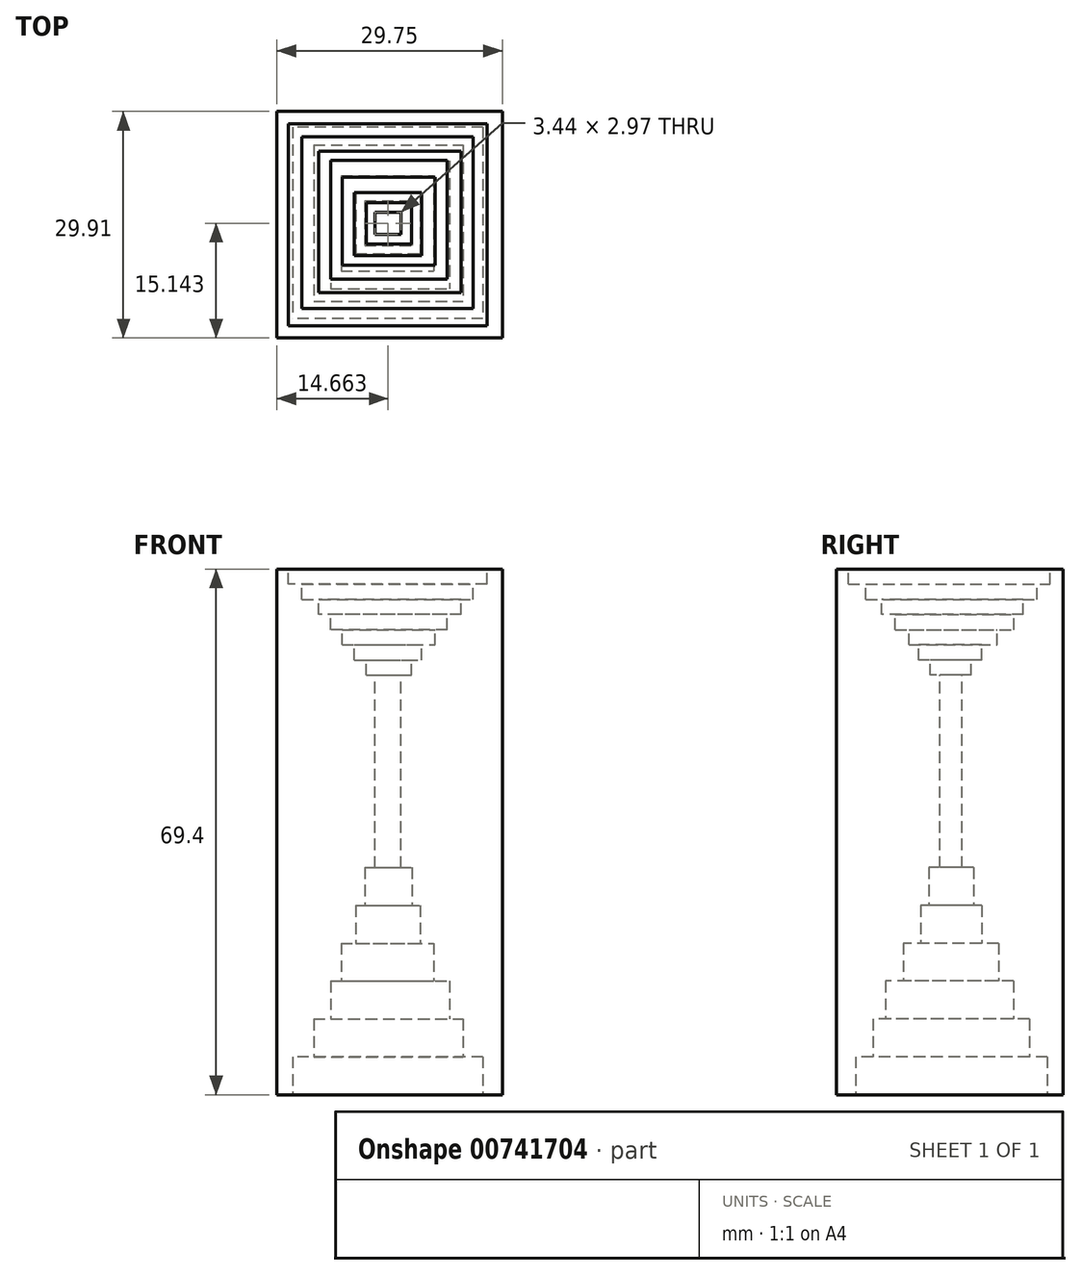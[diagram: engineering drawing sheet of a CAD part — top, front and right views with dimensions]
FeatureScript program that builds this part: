
annotation { "Feature Type Name" : "Feature", "Feature Type Description" : "" }
export const myFeature = defineFeature(function(context is Context, id is Id, definition is map)
    precondition{}
    {
        {
            var Q0;
            Q0=qCreatedBy(makeId("Top.planeOp"),FACE);
            var sketch = newSketch(context, id + "F0", { "sketchPlane" : qUnion([Q0])});
            skLineSegment(sketch, "E0.bottom", {"start": v(11.57, -13.66) * mm, "end": v(41.32, -13.66) * mm});
            skLineSegment(sketch, "E0.top", {"start": v(11.57, 16.25) * mm, "end": v(41.32, 16.25) * mm});
            skLineSegment(sketch, "E0.left", {"start": v(11.57, -13.66) * mm, "end": v(11.57, 16.25) * mm});
            skLineSegment(sketch, "E0.right", {"start": v(41.32, -13.66) * mm, "end": v(41.32, 16.25) * mm});
            skSolve(sketch);
        }
        {
            var Q0;
            Q0=makeQuery(id+"F0.imprint","IMPRINT",FACE,{"disambiguationData":[TD([[makeQuery(id+"F0.imprint","IMPRINT",EDGE,{"derivedFrom":sQuery(id+"F0.wireOp",EDGE,"E0.bottom")}),1.0]])]});
            extrude(context, id + "F1", {"entities" : qUnion([Q0]), "depth" : 69.4 * mm, "offsetDistance" : 25 * mm});
        }
        {
            var Q0;
            Q0=makeQuery(id+"F1.opExtrude","CAP_FACE",FACE,{"disambiguationData":[OSD([sQuery(id+"F0.wireOp",EDGE,"E0.bottom"),sQuery(id+"F0.wireOp",EDGE,"E0.top"),sQuery(id+"F0.wireOp",EDGE,"E0.left"),sQuery(id+"F0.wireOp",EDGE,"E0.right")])],"isStart":false});
            var sketch = newSketch(context, id + "F2", { "sketchPlane" : qUnion([Q0])});
            skLineSegment(sketch, "E1.bottom", {"start": v(39.29, -12.06) * mm, "end": v(13.06, -12.06) * mm});
            skLineSegment(sketch, "E1.top", {"start": v(39.29, 14.6) * mm, "end": v(13.06, 14.6) * mm});
            skLineSegment(sketch, "E1.left", {"start": v(39.29, -12.06) * mm, "end": v(39.29, 14.6) * mm});
            skLineSegment(sketch, "E1.right", {"start": v(13.06, -12.06) * mm, "end": v(13.06, 14.6) * mm});
            skSolve(sketch);
        }
        {
            var Q0;
            Q0=makeQuery(id+"F2.imprint","IMPRINT",FACE,{"disambiguationData":[TD([[makeQuery(id+"F2.imprint","IMPRINT",EDGE,{"derivedFrom":sQuery(id+"F2.wireOp",EDGE,"E1.bottom")}),-1.0]])]});
            extrude(context, id + "F3", {"entities" : qUnion([Q0]), "operationType" : NewBodyOperationType.REMOVE, "oppositeDirection" : true, "depth" : 2 * mm, "offsetDistance" : 25 * mm});
        }
        {
            var Q0;
            Q0=makeQuery(id+"F3.boolean.opBoolean","COPY",FACE,{"derivedFrom":makeQuery(id+"F3.opExtrude","CAP_FACE",FACE,{"disambiguationData":[OSD([sQuery(id+"F2.wireOp",EDGE,"E1.bottom"),sQuery(id+"F2.wireOp",EDGE,"E1.top"),sQuery(id+"F2.wireOp",EDGE,"E1.left"),sQuery(id+"F2.wireOp",EDGE,"E1.right")])],"isStart":false})});
            var sketch = newSketch(context, id + "F4", { "sketchPlane" : qUnion([Q0])});
            skLineSegment(sketch, "E2.bottom", {"start": v(14.87, -9.76) * mm, "end": v(37.5, -9.76) * mm});
            skLineSegment(sketch, "E2.top", {"start": v(14.87, 12.88) * mm, "end": v(37.5, 12.88) * mm});
            skLineSegment(sketch, "E2.left", {"start": v(14.87, -9.76) * mm, "end": v(14.87, 12.88) * mm});
            skLineSegment(sketch, "E2.right", {"start": v(37.5, -9.76) * mm, "end": v(37.5, 12.88) * mm});
            skSolve(sketch);
        }
        {
            var Q0;
            Q0=makeQuery(id+"F4.imprint","IMPRINT",FACE,{"disambiguationData":[TD([[makeQuery(id+"F4.imprint","IMPRINT",EDGE,{"derivedFrom":sQuery(id+"F4.wireOp",EDGE,"E2.bottom")}),1.0]])]});
            extrude(context, id + "F5", {"entities" : qUnion([Q0]), "operationType" : NewBodyOperationType.REMOVE, "oppositeDirection" : true, "depth" : 2 * mm, "offsetDistance" : 25 * mm});
        }
        {
            var Q0;
            Q0=makeQuery(id+"F5.boolean.opBoolean","COPY",FACE,{"derivedFrom":makeQuery(id+"F5.opExtrude","CAP_FACE",FACE,{"disambiguationData":[OSD([sQuery(id+"F4.wireOp",EDGE,"E2.bottom"),sQuery(id+"F4.wireOp",EDGE,"E2.top"),sQuery(id+"F4.wireOp",EDGE,"E2.left"),sQuery(id+"F4.wireOp",EDGE,"E2.right")])],"isStart":false})});
            var sketch = newSketch(context, id + "F6", { "sketchPlane" : qUnion([Q0])});
            skLineSegment(sketch, "E3.bottom", {"start": v(35.9, 11.02) * mm, "end": v(17.1, 11.02) * mm});
            skLineSegment(sketch, "E3.top", {"start": v(35.9, -7.7) * mm, "end": v(17.1, -7.7) * mm});
            skLineSegment(sketch, "E3.left", {"start": v(35.9, 11.02) * mm, "end": v(35.9, -7.7) * mm});
            skLineSegment(sketch, "E3.right", {"start": v(17.1, 11.02) * mm, "end": v(17.1, -7.7) * mm});
            skSolve(sketch);
        }
        {
            var Q0;
            Q0=makeQuery(id+"F6.imprint","IMPRINT",FACE,{"disambiguationData":[TD([[makeQuery(id+"F6.imprint","IMPRINT",EDGE,{"derivedFrom":sQuery(id+"F6.wireOp",EDGE,"E3.bottom")}),1.0]])]});
            extrude(context, id + "F7", {"entities" : qUnion([Q0]), "operationType" : NewBodyOperationType.REMOVE, "oppositeDirection" : true, "depth" : 2 * mm, "offsetDistance" : 25 * mm});
        }
        {
            var Q0;
            Q0=makeQuery(id+"F7.boolean.opBoolean","COPY",FACE,{"derivedFrom":makeQuery(id+"F7.opExtrude","CAP_FACE",FACE,{"disambiguationData":[OSD([sQuery(id+"F6.wireOp",EDGE,"E3.bottom"),sQuery(id+"F6.wireOp",EDGE,"E3.top"),sQuery(id+"F6.wireOp",EDGE,"E3.left"),sQuery(id+"F6.wireOp",EDGE,"E3.right")])],"isStart":false})});
            var sketch = newSketch(context, id + "F8", { "sketchPlane" : qUnion([Q0])});
            skLineSegment(sketch, "E4.bottom", {"start": v(34.06, -5.88) * mm, "end": v(18.64, -5.88) * mm});
            skLineSegment(sketch, "E4.top", {"start": v(34.06, 9.79) * mm, "end": v(18.64, 9.79) * mm});
            skLineSegment(sketch, "E4.left", {"start": v(34.06, -5.88) * mm, "end": v(34.06, 9.79) * mm});
            skLineSegment(sketch, "E4.right", {"start": v(18.64, -5.88) * mm, "end": v(18.64, 9.79) * mm});
            skSolve(sketch);
        }
        {
            var Q0;
            Q0=makeQuery(id+"F8.imprint","IMPRINT",FACE,{"disambiguationData":[TD([[makeQuery(id+"F8.imprint","IMPRINT",EDGE,{"derivedFrom":sQuery(id+"F8.wireOp",EDGE,"E4.bottom")}),-1.0]])]});
            extrude(context, id + "F9", {"entities" : qUnion([Q0]), "operationType" : NewBodyOperationType.REMOVE, "oppositeDirection" : true, "depth" : 2 * mm, "offsetDistance" : 25 * mm});
        }
        {
            var Q0;
            Q0=makeQuery(id+"F9.boolean.opBoolean","COPY",FACE,{"derivedFrom":makeQuery(id+"F9.opExtrude","CAP_FACE",FACE,{"disambiguationData":[OSD([sQuery(id+"F8.wireOp",EDGE,"E4.bottom"),sQuery(id+"F8.wireOp",EDGE,"E4.top"),sQuery(id+"F8.wireOp",EDGE,"E4.left"),sQuery(id+"F8.wireOp",EDGE,"E4.right")])],"isStart":false})});
            var sketch = newSketch(context, id + "F10", { "sketchPlane" : qUnion([Q0])});
            skLineSegment(sketch, "E5.bottom", {"start": v(20.19, -4.04) * mm, "end": v(32.43, -4.04) * mm});
            skLineSegment(sketch, "E5.top", {"start": v(20.19, 7.55) * mm, "end": v(32.43, 7.55) * mm});
            skLineSegment(sketch, "E5.left", {"start": v(20.19, -4.04) * mm, "end": v(20.19, 7.55) * mm});
            skLineSegment(sketch, "E5.right", {"start": v(32.43, -4.04) * mm, "end": v(32.43, 7.55) * mm});
            skSolve(sketch);
        }
        {
            var Q0;
            Q0=makeQuery(id+"F10.imprint","IMPRINT",FACE,{"disambiguationData":[TD([[makeQuery(id+"F10.imprint","IMPRINT",EDGE,{"derivedFrom":sQuery(id+"F10.wireOp",EDGE,"E5.bottom")}),1.0]])]});
            extrude(context, id + "F11", {"entities" : qUnion([Q0]), "operationType" : NewBodyOperationType.REMOVE, "oppositeDirection" : true, "depth" : 2 * mm, "offsetDistance" : 25 * mm});
        }
        {
            var Q0;
            Q0=makeQuery(id+"F11.boolean.opBoolean","COPY",FACE,{"derivedFrom":makeQuery(id+"F11.opExtrude","CAP_FACE",FACE,{"disambiguationData":[OSD([sQuery(id+"F10.wireOp",EDGE,"E5.bottom"),sQuery(id+"F10.wireOp",EDGE,"E5.top"),sQuery(id+"F10.wireOp",EDGE,"E5.left"),sQuery(id+"F10.wireOp",EDGE,"E5.right")])],"isStart":false})});
            var sketch = newSketch(context, id + "F12", { "sketchPlane" : qUnion([Q0])});
            skLineSegment(sketch, "E6.bottom", {"start": v(21.78, 5.53) * mm, "end": v(30.65, 5.53) * mm});
            skLineSegment(sketch, "E6.top", {"start": v(21.78, -2.78) * mm, "end": v(30.65, -2.78) * mm});
            skLineSegment(sketch, "E6.left", {"start": v(21.78, 5.53) * mm, "end": v(21.78, -2.78) * mm});
            skLineSegment(sketch, "E6.right", {"start": v(30.65, 5.53) * mm, "end": v(30.65, -2.78) * mm});
            skSolve(sketch);
        }
        {
            var Q0;
            Q0=makeQuery(id+"F12.imprint","IMPRINT",FACE,{"disambiguationData":[TD([[makeQuery(id+"F12.imprint","IMPRINT",EDGE,{"derivedFrom":sQuery(id+"F12.wireOp",EDGE,"E6.bottom")}),-1.0]])]});
            extrude(context, id + "F13", {"entities" : qUnion([Q0]), "operationType" : NewBodyOperationType.REMOVE, "oppositeDirection" : true, "depth" : 2 * mm, "offsetDistance" : 25 * mm});
        }
        {
            var Q0;
            Q0=makeQuery(id+"F13.boolean.opBoolean","COPY",FACE,{"derivedFrom":makeQuery(id+"F13.opExtrude","CAP_FACE",FACE,{"disambiguationData":[OSD([sQuery(id+"F12.wireOp",EDGE,"E6.bottom"),sQuery(id+"F12.wireOp",EDGE,"E6.top"),sQuery(id+"F12.wireOp",EDGE,"E6.left"),sQuery(id+"F12.wireOp",EDGE,"E6.right")])],"isStart":false})});
            var sketch = newSketch(context, id + "F14", { "sketchPlane" : qUnion([Q0])});
            skLineSegment(sketch, "E7.bottom", {"start": v(23.38, 4.18) * mm, "end": v(29.33, 4.18) * mm});
            skLineSegment(sketch, "E7.top", {"start": v(23.38, -1.22) * mm, "end": v(29.33, -1.22) * mm});
            skLineSegment(sketch, "E7.left", {"start": v(23.38, 4.18) * mm, "end": v(23.38, -1.22) * mm});
            skLineSegment(sketch, "E7.right", {"start": v(29.33, 4.18) * mm, "end": v(29.33, -1.22) * mm});
            skSolve(sketch);
        }
        {
            var Q0;
            Q0=makeQuery(id+"F14.imprint","IMPRINT",FACE,{"disambiguationData":[TD([[makeQuery(id+"F14.imprint","IMPRINT",EDGE,{"derivedFrom":sQuery(id+"F14.wireOp",EDGE,"E7.bottom")}),-1.0]])]});
            extrude(context, id + "F15", {"entities" : qUnion([Q0]), "operationType" : NewBodyOperationType.REMOVE, "oppositeDirection" : true, "depth" : 2 * mm, "offsetDistance" : 25 * mm});
        }
        {
            var Q0;
            Q0=makeQuery(id+"F15.boolean.opBoolean","COPY",FACE,{"derivedFrom":makeQuery(id+"F15.opExtrude","CAP_FACE",FACE,{"disambiguationData":[OSD([sQuery(id+"F14.wireOp",EDGE,"E7.bottom"),sQuery(id+"F14.wireOp",EDGE,"E7.top"),sQuery(id+"F14.wireOp",EDGE,"E7.left"),sQuery(id+"F14.wireOp",EDGE,"E7.right")])],"isStart":false})});
            var sketch = newSketch(context, id + "F16", { "sketchPlane" : qUnion([Q0])});
            skLineSegment(sketch, "E8.bottom", {"start": v(24.51, 2.97) * mm, "end": v(27.95, 2.97) * mm});
            skLineSegment(sketch, "E8.top", {"start": v(24.51, 0) * mm, "end": v(27.95, 0) * mm});
            skLineSegment(sketch, "E8.left", {"start": v(24.51, 2.97) * mm, "end": v(24.51, 0) * mm});
            skLineSegment(sketch, "E8.right", {"start": v(27.95, 2.97) * mm, "end": v(27.95, 0) * mm});
            skSolve(sketch);
        }
        {
            var Q0;
            Q0=makeQuery(id+"F16.imprint","IMPRINT",FACE,{"disambiguationData":[TD([[makeQuery(id+"F16.imprint","IMPRINT",EDGE,{"derivedFrom":sQuery(id+"F16.wireOp",EDGE,"E8.bottom")}),-1.0]])]});
            extrude(context, id + "F17", {"entities" : qUnion([Q0]), "operationType" : NewBodyOperationType.REMOVE, "endBound" : BoundingType.THROUGH_ALL, "oppositeDirection" : true, "depth" : 25 * mm, "offsetDistance" : 25 * mm});
        }
        {
            var Q0;
            Q0=makeQuery(id+"F1.opExtrude","CAP_FACE",FACE,{"disambiguationData":[OSD([sQuery(id+"F0.wireOp",EDGE,"E0.bottom"),sQuery(id+"F0.wireOp",EDGE,"E0.top"),sQuery(id+"F0.wireOp",EDGE,"E0.left"),sQuery(id+"F0.wireOp",EDGE,"E0.right")])],"isStart":true});
            var sketch = newSketch(context, id + "F18", { "sketchPlane" : qUnion([Q0])});
            skLineSegment(sketch, "E9.bottom", {"start": v(38.76, -14.2) * mm, "end": v(13.65, -14.2) * mm});
            skLineSegment(sketch, "E9.top", {"start": v(38.76, 11.11) * mm, "end": v(13.65, 11.11) * mm});
            skLineSegment(sketch, "E9.left", {"start": v(38.76, -14.2) * mm, "end": v(38.76, 11.11) * mm});
            skLineSegment(sketch, "E9.right", {"start": v(13.65, -14.2) * mm, "end": v(13.65, 11.11) * mm});
            skSolve(sketch);
        }
        {
            var Q0;
            Q0=makeQuery(id+"F18.imprint","IMPRINT",FACE,{"disambiguationData":[TD([[makeQuery(id+"F18.imprint","IMPRINT",EDGE,{"derivedFrom":sQuery(id+"F18.wireOp",EDGE,"E9.bottom")}),-1.0]])]});
            extrude(context, id + "F19", {"entities" : qUnion([Q0]), "operationType" : NewBodyOperationType.REMOVE, "oppositeDirection" : true, "depth" : 5 * mm, "offsetDistance" : 25 * mm});
        }
        {
            var Q0;
            Q0=makeQuery(id+"F19.boolean.opBoolean","COPY",FACE,{"derivedFrom":makeQuery(id+"F19.opExtrude","CAP_FACE",FACE,{"disambiguationData":[OSD([sQuery(id+"F0.wireOp",EDGE,"E0.bottom"),sQuery(id+"F0.wireOp",EDGE,"E0.top"),sQuery(id+"F0.wireOp",EDGE,"E0.left"),sQuery(id+"F0.wireOp",EDGE,"E0.right"),sQuery(id+"F16.wireOp",EDGE,"E8.bottom"),sQuery(id+"F16.wireOp",EDGE,"E8.top"),sQuery(id+"F16.wireOp",EDGE,"E8.left"),sQuery(id+"F16.wireOp",EDGE,"E8.right"),sQuery(id+"F18.wireOp",EDGE,"E9.bottom"),sQuery(id+"F18.wireOp",EDGE,"E9.top"),sQuery(id+"F18.wireOp",EDGE,"E9.left"),sQuery(id+"F18.wireOp",EDGE,"E9.right")])],"isStart":false})});
            var sketch = newSketch(context, id + "F20", { "sketchPlane" : qUnion([Q0])});
            skLineSegment(sketch, "E10.bottom", {"start": v(16.43, -11.84) * mm, "end": v(36.14, -11.84) * mm});
            skLineSegment(sketch, "E10.top", {"start": v(16.43, 8.78) * mm, "end": v(36.14, 8.78) * mm});
            skLineSegment(sketch, "E10.left", {"start": v(16.43, -11.84) * mm, "end": v(16.43, 8.78) * mm});
            skLineSegment(sketch, "E10.right", {"start": v(36.14, -11.84) * mm, "end": v(36.14, 8.78) * mm});
            skSolve(sketch);
        }
        {
            var Q0;
            Q0=makeQuery(id+"F20.imprint","IMPRINT",FACE,{"disambiguationData":[TD([[makeQuery(id+"F20.imprint","IMPRINT",EDGE,{"derivedFrom":sQuery(id+"F20.wireOp",EDGE,"E10.bottom")}),1.0]])]});
            extrude(context, id + "F21", {"entities" : qUnion([Q0]), "operationType" : NewBodyOperationType.REMOVE, "oppositeDirection" : true, "depth" : 5 * mm, "offsetDistance" : 25 * mm});
        }
        {
            var Q0;
            Q0=makeQuery(id+"F21.boolean.opBoolean","COPY",FACE,{"derivedFrom":makeQuery(id+"F21.opExtrude","CAP_FACE",FACE,{"disambiguationData":[OSD([sQuery(id+"F0.wireOp",EDGE,"E0.bottom"),sQuery(id+"F0.wireOp",EDGE,"E0.top"),sQuery(id+"F0.wireOp",EDGE,"E0.left"),sQuery(id+"F0.wireOp",EDGE,"E0.right"),sQuery(id+"F16.wireOp",EDGE,"E8.bottom"),sQuery(id+"F16.wireOp",EDGE,"E8.top"),sQuery(id+"F16.wireOp",EDGE,"E8.left"),sQuery(id+"F16.wireOp",EDGE,"E8.right"),sQuery(id+"F20.wireOp",EDGE,"E10.bottom"),sQuery(id+"F20.wireOp",EDGE,"E10.top"),sQuery(id+"F20.wireOp",EDGE,"E10.left"),sQuery(id+"F20.wireOp",EDGE,"E10.right")])],"isStart":false})});
            var sketch = newSketch(context, id + "F22", { "sketchPlane" : qUnion([Q0])});
            skLineSegment(sketch, "E11.bottom", {"start": v(18.67, -9.73) * mm, "end": v(34.35, -9.73) * mm});
            skLineSegment(sketch, "E11.top", {"start": v(18.67, 7.14) * mm, "end": v(34.35, 7.14) * mm});
            skLineSegment(sketch, "E11.left", {"start": v(18.67, -9.73) * mm, "end": v(18.67, 7.14) * mm});
            skLineSegment(sketch, "E11.right", {"start": v(34.35, -9.73) * mm, "end": v(34.35, 7.14) * mm});
            skSolve(sketch);
        }
        {
            var Q0;
            Q0=makeQuery(id+"F22.imprint","IMPRINT",FACE,{"disambiguationData":[TD([[makeQuery(id+"F22.imprint","IMPRINT",EDGE,{"derivedFrom":sQuery(id+"F22.wireOp",EDGE,"E11.bottom")}),1.0]])]});
            extrude(context, id + "F23", {"entities" : qUnion([Q0]), "operationType" : NewBodyOperationType.REMOVE, "oppositeDirection" : true, "depth" : 5 * mm, "offsetDistance" : 25 * mm});
        }
        {
            var Q0;
            Q0=makeQuery(id+"F23.boolean.opBoolean","COPY",FACE,{"derivedFrom":makeQuery(id+"F23.opExtrude","CAP_FACE",FACE,{"disambiguationData":[OSD([sQuery(id+"F0.wireOp",EDGE,"E0.bottom"),sQuery(id+"F0.wireOp",EDGE,"E0.top"),sQuery(id+"F0.wireOp",EDGE,"E0.left"),sQuery(id+"F0.wireOp",EDGE,"E0.right"),sQuery(id+"F16.wireOp",EDGE,"E8.bottom"),sQuery(id+"F16.wireOp",EDGE,"E8.top"),sQuery(id+"F16.wireOp",EDGE,"E8.left"),sQuery(id+"F16.wireOp",EDGE,"E8.right"),sQuery(id+"F22.wireOp",EDGE,"E11.bottom"),sQuery(id+"F22.wireOp",EDGE,"E11.top"),sQuery(id+"F22.wireOp",EDGE,"E11.left"),sQuery(id+"F22.wireOp",EDGE,"E11.right")])],"isStart":false})});
            var sketch = newSketch(context, id + "F24", { "sketchPlane" : qUnion([Q0])});
            skLineSegment(sketch, "E12.bottom", {"start": v(20.04, -7.76) * mm, "end": v(32.29, -7.76) * mm});
            skLineSegment(sketch, "E12.top", {"start": v(20.04, 4.83) * mm, "end": v(32.29, 4.83) * mm});
            skLineSegment(sketch, "E12.left", {"start": v(20.04, -7.76) * mm, "end": v(20.04, 4.83) * mm});
            skLineSegment(sketch, "E12.right", {"start": v(32.29, -7.76) * mm, "end": v(32.29, 4.83) * mm});
            skSolve(sketch);
        }
        {
            var Q0;
            Q0=makeQuery(id+"F24.imprint","IMPRINT",FACE,{"disambiguationData":[TD([[makeQuery(id+"F24.imprint","IMPRINT",EDGE,{"derivedFrom":sQuery(id+"F24.wireOp",EDGE,"E12.bottom")}),1.0]])]});
            extrude(context, id + "F25", {"entities" : qUnion([Q0]), "operationType" : NewBodyOperationType.REMOVE, "oppositeDirection" : true, "depth" : 5 * mm, "offsetDistance" : 25 * mm});
        }
        {
            var Q0;
            Q0=makeQuery(id+"F25.boolean.opBoolean","COPY",FACE,{"derivedFrom":makeQuery(id+"F25.opExtrude","CAP_FACE",FACE,{"disambiguationData":[OSD([sQuery(id+"F0.wireOp",EDGE,"E0.bottom"),sQuery(id+"F0.wireOp",EDGE,"E0.top"),sQuery(id+"F0.wireOp",EDGE,"E0.left"),sQuery(id+"F0.wireOp",EDGE,"E0.right"),sQuery(id+"F16.wireOp",EDGE,"E8.bottom"),sQuery(id+"F16.wireOp",EDGE,"E8.top"),sQuery(id+"F16.wireOp",EDGE,"E8.left"),sQuery(id+"F16.wireOp",EDGE,"E8.right"),sQuery(id+"F24.wireOp",EDGE,"E12.bottom"),sQuery(id+"F24.wireOp",EDGE,"E12.top"),sQuery(id+"F24.wireOp",EDGE,"E12.left"),sQuery(id+"F24.wireOp",EDGE,"E12.right")])],"isStart":false})});
            var sketch = newSketch(context, id + "F26", { "sketchPlane" : qUnion([Q0])});
            skLineSegment(sketch, "E13.bottom", {"start": v(21.96, -5.55) * mm, "end": v(30.49, -5.55) * mm});
            skLineSegment(sketch, "E13.top", {"start": v(21.96, 2.5) * mm, "end": v(30.49, 2.5) * mm});
            skLineSegment(sketch, "E13.left", {"start": v(21.96, -5.55) * mm, "end": v(21.96, 2.5) * mm});
            skLineSegment(sketch, "E13.right", {"start": v(30.49, -5.55) * mm, "end": v(30.49, 2.5) * mm});
            skSolve(sketch);
        }
        {
            var Q0;
            Q0=makeQuery(id+"F26.imprint","IMPRINT",FACE,{"disambiguationData":[TD([[makeQuery(id+"F26.imprint","IMPRINT",EDGE,{"derivedFrom":sQuery(id+"F26.wireOp",EDGE,"E13.bottom")}),1.0]])]});
            extrude(context, id + "F27", {"entities" : qUnion([Q0]), "operationType" : NewBodyOperationType.REMOVE, "oppositeDirection" : true, "depth" : 5 * mm, "offsetDistance" : 25 * mm});
        }
        {
            var Q0;
            Q0=makeQuery(id+"F27.boolean.opBoolean","COPY",FACE,{"derivedFrom":makeQuery(id+"F27.opExtrude","CAP_FACE",FACE,{"disambiguationData":[OSD([sQuery(id+"F0.wireOp",EDGE,"E0.bottom"),sQuery(id+"F0.wireOp",EDGE,"E0.top"),sQuery(id+"F0.wireOp",EDGE,"E0.left"),sQuery(id+"F0.wireOp",EDGE,"E0.right"),sQuery(id+"F16.wireOp",EDGE,"E8.bottom"),sQuery(id+"F16.wireOp",EDGE,"E8.top"),sQuery(id+"F16.wireOp",EDGE,"E8.left"),sQuery(id+"F16.wireOp",EDGE,"E8.right"),sQuery(id+"F26.wireOp",EDGE,"E13.bottom"),sQuery(id+"F26.wireOp",EDGE,"E13.top"),sQuery(id+"F26.wireOp",EDGE,"E13.left"),sQuery(id+"F26.wireOp",EDGE,"E13.right")])],"isStart":false})});
            var sketch = newSketch(context, id + "F28", { "sketchPlane" : qUnion([Q0])});
            skLineSegment(sketch, "E14.bottom", {"start": v(23.15, -4.49) * mm, "end": v(29.41, -4.49) * mm});
            skLineSegment(sketch, "E14.top", {"start": v(23.15, 1.41) * mm, "end": v(29.41, 1.41) * mm});
            skLineSegment(sketch, "E14.left", {"start": v(23.15, -4.49) * mm, "end": v(23.15, 1.41) * mm});
            skLineSegment(sketch, "E14.right", {"start": v(29.41, -4.49) * mm, "end": v(29.41, 1.41) * mm});
            skSolve(sketch);
        }
        {
            var Q0;
            Q0=makeQuery(id+"F28.imprint","IMPRINT",FACE,{"disambiguationData":[TD([[makeQuery(id+"F28.imprint","IMPRINT",EDGE,{"derivedFrom":sQuery(id+"F28.wireOp",EDGE,"E14.bottom")}),1.0]])]});
            var Q1;
            Q1=sQuery(id+"F28.wireOp",EDGE,"E14.left");
            var Q2;
            Q2=sQuery(id+"F28.wireOp",EDGE,"E14.bottom");
            var Q3;
            Q3=sQuery(id+"F28.wireOp",EDGE,"E14.right");
            var Q4;
            Q4=sQuery(id+"F28.wireOp",EDGE,"E14.top");
            extrude(context, id + "F29", {"entities" : qUnion([Q0]), "operationType" : NewBodyOperationType.REMOVE, "surfaceEntities" : qUnion([Q1, Q2, Q3, Q4]), "oppositeDirection" : true, "depth" : 5 * mm, "offsetDistance" : 25 * mm});
        }
    });
